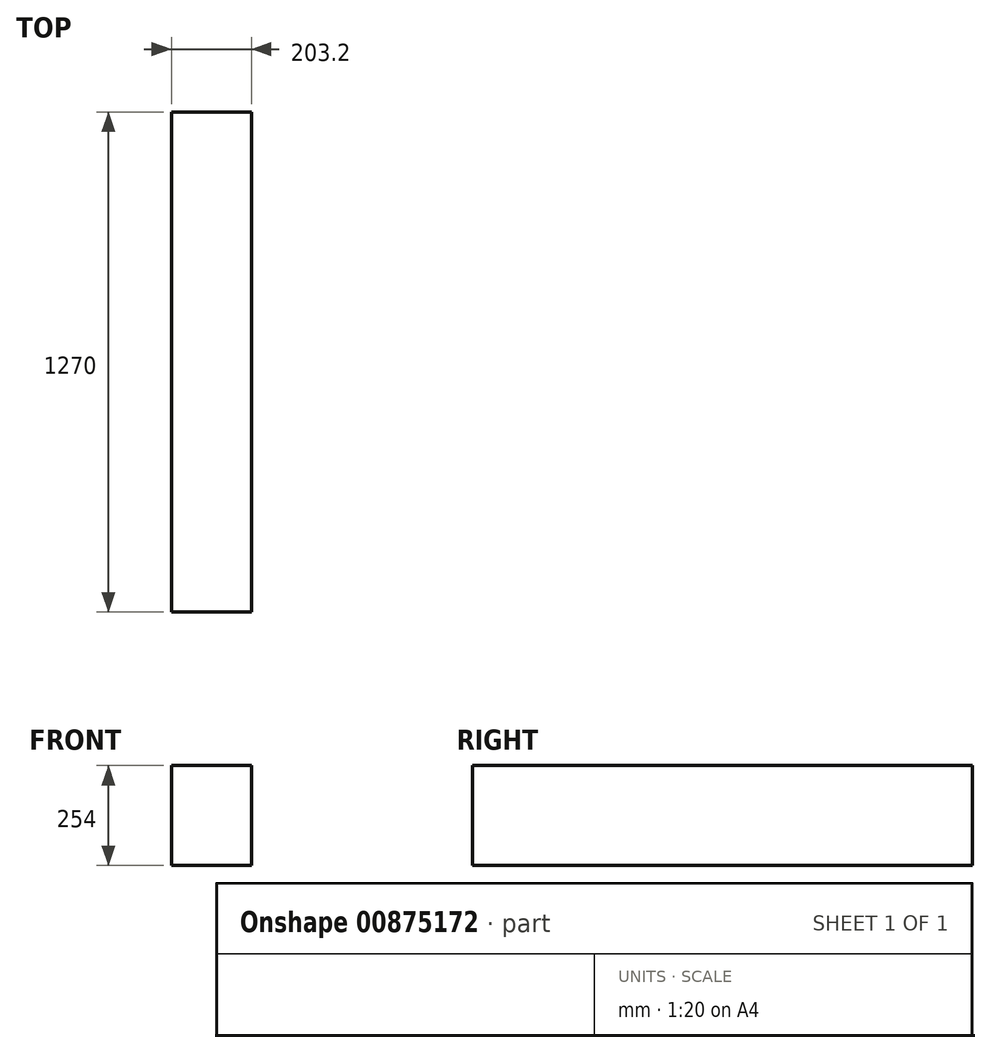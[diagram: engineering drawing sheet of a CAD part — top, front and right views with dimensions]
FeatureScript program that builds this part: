
annotation { "Feature Type Name" : "Feature", "Feature Type Description" : "" }
export const myFeature = defineFeature(function(context is Context, id is Id, definition is map)
    precondition{}
    {
        {
            var Q0;
            Q0=qCreatedBy(makeId("Front.planeOp"),FACE);
            var sketch = newSketch(context, id + "F0", { "sketchPlane" : qUnion([Q0])});
            skLineSegment(sketch, "E0.bottom", {"start": v(-271.3, 262.87) * mm, "end": v(-68.1, 262.87) * mm});
            skLineSegment(sketch, "E0.top", {"start": v(-271.3, 8.87) * mm, "end": v(-68.1, 8.87) * mm});
            skLineSegment(sketch, "E0.left", {"start": v(-271.3, 262.87) * mm, "end": v(-271.3, 8.87) * mm});
            skLineSegment(sketch, "E0.right", {"start": v(-68.1, 262.87) * mm, "end": v(-68.1, 8.87) * mm});
            skSolve(sketch);
        }
        {
            var Q0;
            Q0=makeQuery(id+"F0.imprint","IMPRINT",FACE,{"disambiguationData":[TD([[makeQuery(id+"F0.imprint","IMPRINT",EDGE,{"derivedFrom":sQuery(id+"F0.wireOp",EDGE,"E0.bottom")}),-1.0]])]});
            extrude(context, id + "F1", {"entities" : qUnion([Q0]), "depth" : 1270 * mm, "offsetDistance" : 25.4 * mm});
        }
    });
